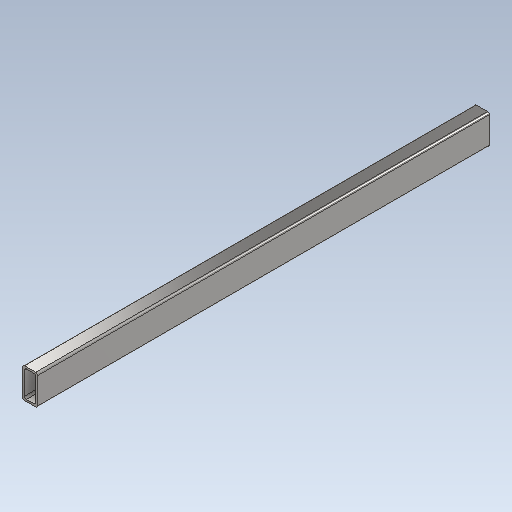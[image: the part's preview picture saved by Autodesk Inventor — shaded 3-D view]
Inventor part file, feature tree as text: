
AUTODESK INVENTOR PART (.ipt)
format: ipt  version: 2020 (Build 240168000, 168)  size: 128,000 bytes
history: native  units: in
note: dims shown in document units (in); Inventor stores cm internally (conversion verified against a paired STEP export)
features: extrude x1, sketch x1
ambient origin geometry x8: Origin, YZ Plane, XZ Plane, XY Plane, X Axis, Y Axis, Z Axis, Center Point
bodies: Solid1 (feature_tree)
feature tree (2):
  extrude  "Extrusion1"  Depth=1.0in
  sketch  "Sketch1"  dims[d0=2.0in d1=1.0in d2=0.125in d3=0.125in d4=0.125in d5=0.125in d6=0.125in d7=0.125in d8=0.125in d9=0.125in d10=0.125in d11=30.0in d12=0.0in]
